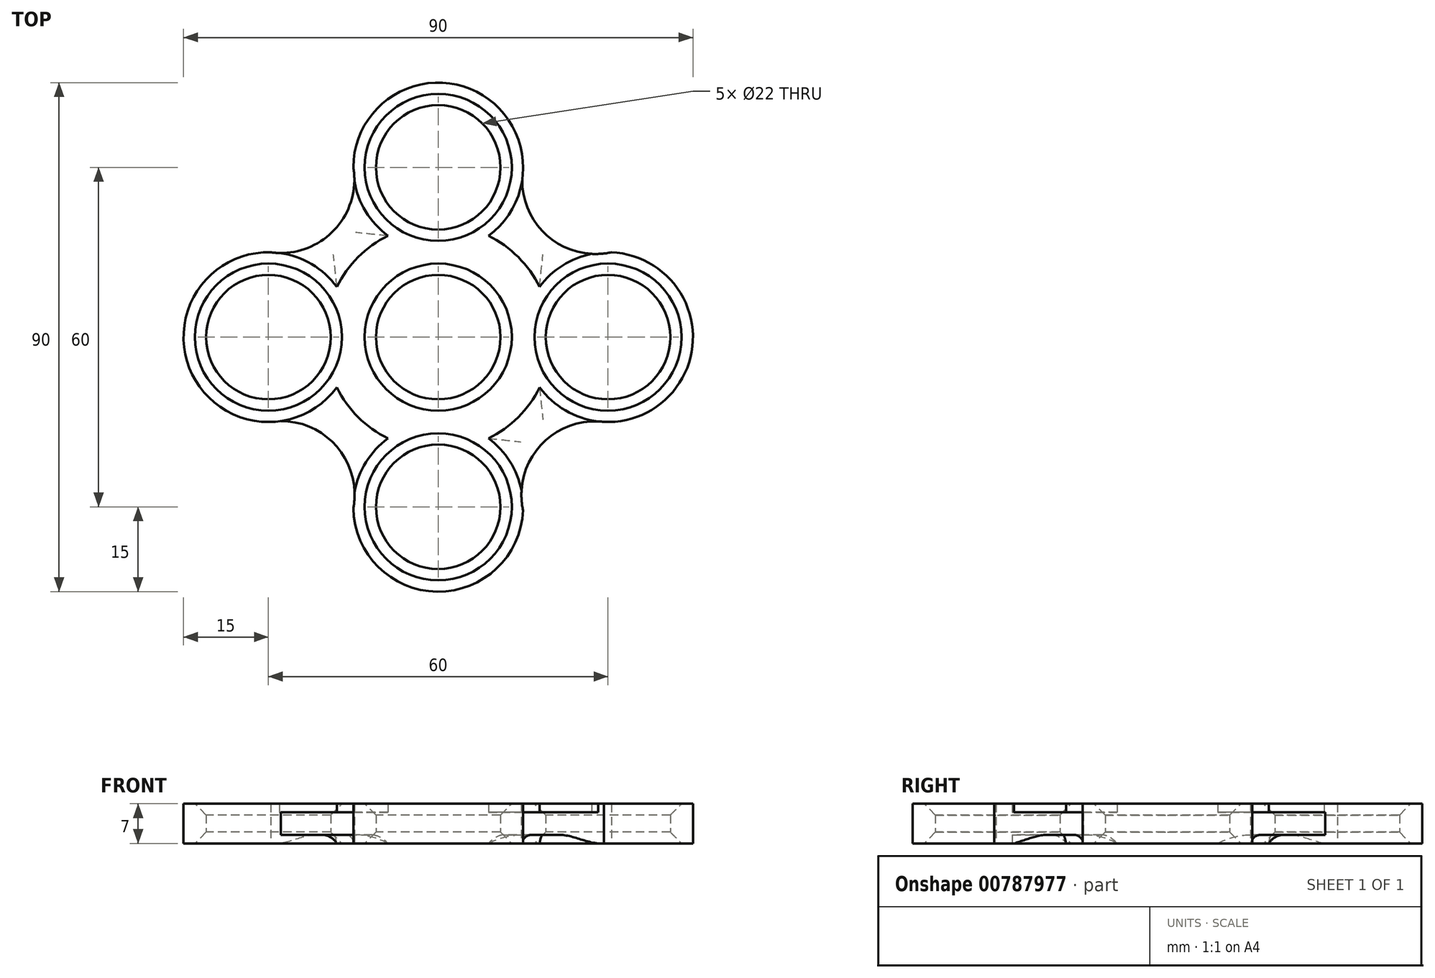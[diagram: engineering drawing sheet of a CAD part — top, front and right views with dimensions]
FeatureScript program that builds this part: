
annotation { "Feature Type Name" : "Feature", "Feature Type Description" : "" }
export const myFeature = defineFeature(function(context is Context, id is Id, definition is map)
    precondition{}
    {
        {
            var Q0;
            Q0=qCreatedBy(makeId("Top.planeOp"),FACE);
            var sketch = newSketch(context, id + "F0", { "sketchPlane" : qUnion([Q0])});
            skCircle(sketch, "E0", {"center": v(0, 0) * mm, "radius": 11 * mm});
            skCircle(sketch, "E1", {"center": v(0, 0) * mm, "radius": 20 * mm});
            skCircle(sketch, "E2", {"center": v(-30, 0) * mm, "radius": 15 * mm});
            skCircle(sketch, "E3", {"center": v(30, 0) * mm, "radius": 15 * mm});
            skCircle(sketch, "E4", {"center": v(0, 30) * mm, "radius": 15 * mm});
            skCircle(sketch, "E5", {"center": v(0, -30) * mm, "radius": 15 * mm});
            skArc(sketch, "E6", {"start": v(-29.62, 15) * mm, "mid": v(-18.5, 18.81) * mm, "end": v(-15, 30.05) * mm});
            skArc(sketch, "E7", {"start": v(14.85, 27.87) * mm, "mid": v(19.61, 17.64) * mm, "end": v(30.58, 14.99) * mm});
            skArc(sketch, "E8", {"start": v(29.26, -14.98) * mm, "mid": v(18.1, -19.12) * mm, "end": v(14.99, -30.62) * mm});
            skArc(sketch, "E9", {"start": v(-15, -30.26) * mm, "mid": v(-17.77, -19.53) * mm, "end": v(-27.82, -14.84) * mm});
            skCircle(sketch, "E10", {"center": v(0, 30) * mm, "radius": 11 * mm});
            skCircle(sketch, "E11", {"center": v(-30, 0) * mm, "radius": 11 * mm});
            skCircle(sketch, "E12", {"center": v(0, -30) * mm, "radius": 11 * mm});
            skCircle(sketch, "E13", {"center": v(30, 0) * mm, "radius": 11 * mm});
            skSolve(sketch);
        }
        {
            var Q0;
            Q0=makeQuery(id+"F0.imprint","IMPRINT",FACE,{"disambiguationData":[TD([[makeQuery(id+"F0.imprint","IMPRINT",EDGE,{"derivedFrom":sQuery(id+"F0.wireOp",EDGE,"E0")}),-1.0]])]});
            var Q1;
            {var subQ0=sQuery(id+"F0.wireOp",EDGE,"E2");var subQ3=sQuery(id+"F0.wireOp",EDGE,"E1");var subQ4=makeQuery(id+"F0.imprint","INTERSECT",VERTEX,{"disambiguationData":[OD(0.0)],"derivedFrom":[subQ3,subQ0]});Q1=makeQuery(id+"F0.imprint","IMPRINT",FACE,{"disambiguationData":[TD([[makeQuery(id+"F0.imprint","IMPRINT",EDGE,{"disambiguationData":[TD([[subQ4,-1.0]])],"derivedFrom":subQ3}),-1.0]])]});}
            var Q2;
            {var subQ0=sQuery(id+"F0.wireOp",EDGE,"E2");var subQ1=sQuery(id+"F0.wireOp",EDGE,"E1");var subQ2=makeQuery(id+"F0.imprint","INTERSECT",VERTEX,{"disambiguationData":[OD(0.0)],"derivedFrom":[subQ1,subQ0]});Q2=makeQuery(id+"F0.imprint","IMPRINT",FACE,{"disambiguationData":[TD([[makeQuery(id+"F0.imprint","IMPRINT",EDGE,{"disambiguationData":[TD([[subQ2,-1.0]])],"derivedFrom":subQ1}),1.0]])]});}
            var Q3;
            {var subQ0=sQuery(id+"F0.wireOp",EDGE,"E4");var subQ2=sQuery(id+"F0.wireOp",EDGE,"E1");var subQ7=makeQuery(id+"F0.imprint","INTERSECT",VERTEX,{"disambiguationData":[OD(0.0)],"derivedFrom":[subQ2,subQ0]});Q3=makeQuery(id+"F0.imprint","IMPRINT",FACE,{"disambiguationData":[TD([[makeQuery(id+"F0.imprint","IMPRINT",EDGE,{"disambiguationData":[TD([[subQ7,-1.0]])],"derivedFrom":subQ2}),-1.0]])]});}
            var Q4;
            {var subQ0=sQuery(id+"F0.wireOp",EDGE,"E4");var subQ1=sQuery(id+"F0.wireOp",EDGE,"E1");var subQ2=makeQuery(id+"F0.imprint","INTERSECT",VERTEX,{"disambiguationData":[OD(0.0)],"derivedFrom":[subQ1,subQ0]});Q4=makeQuery(id+"F0.imprint","IMPRINT",FACE,{"disambiguationData":[TD([[makeQuery(id+"F0.imprint","IMPRINT",EDGE,{"disambiguationData":[TD([[subQ2,-1.0]])],"derivedFrom":subQ1}),1.0]])]});}
            var Q5;
            {var subQ0=sQuery(id+"F0.wireOp",EDGE,"E3");var subQ2=sQuery(id+"F0.wireOp",EDGE,"E1");var subQ6=makeQuery(id+"F0.imprint","INTERSECT",VERTEX,{"disambiguationData":[OD(0.0)],"derivedFrom":[subQ2,subQ0]});Q5=makeQuery(id+"F0.imprint","IMPRINT",FACE,{"disambiguationData":[TD([[makeQuery(id+"F0.imprint","IMPRINT",EDGE,{"disambiguationData":[TD([[subQ6,1.0]])],"derivedFrom":subQ2}),-1.0]])]});}
            var Q6;
            {var subQ0=sQuery(id+"F0.wireOp",EDGE,"E3");var subQ1=sQuery(id+"F0.wireOp",EDGE,"E1");var subQ2=makeQuery(id+"F0.imprint","INTERSECT",VERTEX,{"disambiguationData":[OD(0.0)],"derivedFrom":[subQ1,subQ0]});Q6=makeQuery(id+"F0.imprint","IMPRINT",FACE,{"disambiguationData":[TD([[makeQuery(id+"F0.imprint","IMPRINT",EDGE,{"disambiguationData":[TD([[subQ2,1.0]])],"derivedFrom":subQ1}),1.0]])]});}
            var Q7;
            {var subQ1=sQuery(id+"F0.wireOp",EDGE,"E5");var subQ3=sQuery(id+"F0.wireOp",EDGE,"E1");var subQ4=makeQuery(id+"F0.imprint","INTERSECT",VERTEX,{"disambiguationData":[OD(0.0)],"derivedFrom":[subQ3,subQ1]});Q7=makeQuery(id+"F0.imprint","IMPRINT",FACE,{"disambiguationData":[TD([[makeQuery(id+"F0.imprint","IMPRINT",EDGE,{"disambiguationData":[TD([[subQ4,-1.0]])],"derivedFrom":subQ3}),-1.0]])]});}
            var Q8;
            {var subQ0=sQuery(id+"F0.wireOp",EDGE,"E5");var subQ1=sQuery(id+"F0.wireOp",EDGE,"E1");var subQ2=makeQuery(id+"F0.imprint","INTERSECT",VERTEX,{"disambiguationData":[OD(0.0)],"derivedFrom":[subQ1,subQ0]});Q8=makeQuery(id+"F0.imprint","IMPRINT",FACE,{"disambiguationData":[TD([[makeQuery(id+"F0.imprint","IMPRINT",EDGE,{"disambiguationData":[TD([[subQ2,-1.0]])],"derivedFrom":subQ1}),1.0]])]});}
            extrude(context, id + "F1", {"entities" : qUnion([Q0, Q1, Q2, Q3, Q4, Q5, Q6, Q7, Q8]), "depth" : 7 * mm, "offsetDistance" : 25 * mm});
        }
        {
            var Q0;
            {var subQ0=sQuery(id+"F0.wireOp",EDGE,"E2");var subQ1=sQuery(id+"F0.wireOp",EDGE,"E1");var subQ2=makeQuery(id+"F0.imprint","INTERSECT",VERTEX,{"disambiguationData":[OD(1.0)],"derivedFrom":[subQ1,subQ0]});Q0=makeQuery(id+"F0.imprint","IMPRINT",FACE,{"disambiguationData":[TD([[makeQuery(id+"F0.imprint","IMPRINT",EDGE,{"disambiguationData":[TD([[subQ2,-1.0]])],"derivedFrom":subQ1}),-1.0]])]});}
            var Q1;
            {var subQ5=sQuery(id+"F0.wireOp",EDGE,"E6");Q1=makeQuery(id+"F0.imprint","IMPRINT",FACE,{"disambiguationData":[TD([[makeQuery(id+"F0.imprint","IMPRINT",EDGE,{"derivedFrom":subQ5}),-1.0]])]});}
            var Q2;
            {var subQ0=sQuery(id+"F0.wireOp",EDGE,"E3");var subQ1=sQuery(id+"F0.wireOp",EDGE,"E1");var subQ2=makeQuery(id+"F0.imprint","INTERSECT",VERTEX,{"disambiguationData":[OD(0.0)],"derivedFrom":[subQ1,subQ0]});Q2=makeQuery(id+"F0.imprint","IMPRINT",FACE,{"disambiguationData":[TD([[makeQuery(id+"F0.imprint","IMPRINT",EDGE,{"disambiguationData":[TD([[subQ2,-1.0]])],"derivedFrom":subQ1}),-1.0]])]});}
            var Q3;
            {var subQ0=sQuery(id+"F0.wireOp",EDGE,"E5");var subQ1=sQuery(id+"F0.wireOp",EDGE,"E1");var subQ2=makeQuery(id+"F0.imprint","INTERSECT",VERTEX,{"disambiguationData":[OD(1.0)],"derivedFrom":[subQ1,subQ0]});Q3=makeQuery(id+"F0.imprint","IMPRINT",FACE,{"disambiguationData":[TD([[makeQuery(id+"F0.imprint","IMPRINT",EDGE,{"disambiguationData":[TD([[subQ2,-1.0]])],"derivedFrom":subQ1}),-1.0]])]});}
            extrude(context, id + "F2", {"entities" : qUnion([Q0, Q1, Q2, Q3]), "operationType" : NewBodyOperationType.ADD, "surfaceOperationType" : NewSurfaceOperationType.ADD, "depth" : 5.5 * mm, "offsetDistance" : 25 * mm, "hasSecondDirection" : true, "secondDirectionOppositeDirection" : false, "secondDirectionDepth" : 1.5 * mm});
        }
        {
            var Q0;
            {var subQ0=sQuery(id+"F0.wireOp",EDGE,"E1");Q0=makeQuery(id+"F2.opExtrude","CAP_EDGE",EDGE,{"disambiguationData":[OSD([subQ0]),TDD([makeQuery(id+"F0.imprint","IMPRINT",EDGE,{"disambiguationData":[TD([[makeQuery(id+"F0.imprint","INTERSECT",VERTEX,{"disambiguationData":[OD(1.0)],"derivedFrom":[subQ0,sQuery(id+"F0.wireOp",EDGE,"E2")]}),-1.0]])],"derivedFrom":subQ0})])],"isStart":false});}
            var Q1;
            {var subQ0=sQuery(id+"F0.wireOp",EDGE,"E1");Q1=makeQuery(id+"F2.opExtrude","CAP_EDGE",EDGE,{"disambiguationData":[OSD([subQ0]),TDD([makeQuery(id+"F0.imprint","IMPRINT",EDGE,{"disambiguationData":[TD([[makeQuery(id+"F0.imprint","INTERSECT",VERTEX,{"disambiguationData":[OD(1.0)],"derivedFrom":[subQ0,sQuery(id+"F0.wireOp",EDGE,"E2")]}),-1.0]])],"derivedFrom":subQ0})])],"isStart":true});}
            var Q2;
            {var subQ0=sQuery(id+"F0.wireOp",EDGE,"E1");Q2=makeQuery(id+"F2.opExtrude","CAP_EDGE",EDGE,{"disambiguationData":[OSD([subQ0]),TDD([makeQuery(id+"F0.imprint","IMPRINT",EDGE,{"disambiguationData":[TD([[makeQuery(id+"F0.imprint","INTERSECT",VERTEX,{"disambiguationData":[OD(1.0)],"derivedFrom":[subQ0,sQuery(id+"F0.wireOp",EDGE,"E4")]}),-1.0]])],"derivedFrom":subQ0})])],"isStart":false});}
            var Q3;
            {var subQ0=sQuery(id+"F0.wireOp",EDGE,"E1");Q3=makeQuery(id+"F2.opExtrude","CAP_EDGE",EDGE,{"disambiguationData":[OSD([subQ0]),TDD([makeQuery(id+"F0.imprint","IMPRINT",EDGE,{"disambiguationData":[TD([[makeQuery(id+"F0.imprint","INTERSECT",VERTEX,{"disambiguationData":[OD(1.0)],"derivedFrom":[subQ0,sQuery(id+"F0.wireOp",EDGE,"E4")]}),-1.0]])],"derivedFrom":subQ0})])],"isStart":true});}
            var Q4;
            {var subQ0=sQuery(id+"F0.wireOp",EDGE,"E1");Q4=makeQuery(id+"F2.opExtrude","CAP_EDGE",EDGE,{"disambiguationData":[OSD([subQ0]),TDD([makeQuery(id+"F0.imprint","IMPRINT",EDGE,{"disambiguationData":[TD([[makeQuery(id+"F0.imprint","INTERSECT",VERTEX,{"disambiguationData":[OD(0.0)],"derivedFrom":[subQ0,sQuery(id+"F0.wireOp",EDGE,"E3")]}),-1.0]])],"derivedFrom":subQ0})])],"isStart":false});}
            var Q5;
            {var subQ0=sQuery(id+"F0.wireOp",EDGE,"E1");Q5=makeQuery(id+"F2.opExtrude","CAP_EDGE",EDGE,{"disambiguationData":[OSD([subQ0]),TDD([makeQuery(id+"F0.imprint","IMPRINT",EDGE,{"disambiguationData":[TD([[makeQuery(id+"F0.imprint","INTERSECT",VERTEX,{"disambiguationData":[OD(0.0)],"derivedFrom":[subQ0,sQuery(id+"F0.wireOp",EDGE,"E3")]}),-1.0]])],"derivedFrom":subQ0})])],"isStart":true});}
            var Q6;
            {var subQ0=sQuery(id+"F0.wireOp",EDGE,"E1");Q6=makeQuery(id+"F2.opExtrude","CAP_EDGE",EDGE,{"disambiguationData":[OSD([subQ0]),TDD([makeQuery(id+"F0.imprint","IMPRINT",EDGE,{"disambiguationData":[TD([[makeQuery(id+"F0.imprint","INTERSECT",VERTEX,{"disambiguationData":[OD(1.0)],"derivedFrom":[subQ0,sQuery(id+"F0.wireOp",EDGE,"E5")]}),-1.0]])],"derivedFrom":subQ0})])],"isStart":false});}
            var Q7;
            {var subQ0=sQuery(id+"F0.wireOp",EDGE,"E1");Q7=makeQuery(id+"F2.opExtrude","CAP_EDGE",EDGE,{"disambiguationData":[OSD([subQ0]),TDD([makeQuery(id+"F0.imprint","IMPRINT",EDGE,{"disambiguationData":[TD([[makeQuery(id+"F0.imprint","INTERSECT",VERTEX,{"disambiguationData":[OD(1.0)],"derivedFrom":[subQ0,sQuery(id+"F0.wireOp",EDGE,"E5")]}),-1.0]])],"derivedFrom":subQ0})])],"isStart":true});}
            var Q8;
            {var subQ0=sQuery(id+"F0.wireOp",EDGE,"E5");Q8=makeQuery(id+"F2.opExtrude","CAP_EDGE",EDGE,{"disambiguationData":[OSD([subQ0]),TDD([makeQuery(id+"F0.imprint","IMPRINT",EDGE,{"disambiguationData":[TD([[makeQuery(id+"F0.imprint","INTERSECT",VERTEX,{"disambiguationData":[OD(1.0)],"derivedFrom":[subQ0,sQuery(id+"F0.wireOp",EDGE,"E8")]}),-1.0]])],"derivedFrom":subQ0})])],"isStart":false});}
            var Q9;
            {var subQ0=sQuery(id+"F0.wireOp",EDGE,"E3");Q9=makeQuery(id+"F2.opExtrude","CAP_EDGE",EDGE,{"disambiguationData":[OSD([subQ0]),TDD([makeQuery(id+"F0.imprint","IMPRINT",EDGE,{"disambiguationData":[TD([[makeQuery(id+"F0.imprint","INTERSECT",VERTEX,{"derivedFrom":[subQ0,sQuery(id+"F0.wireOp",EDGE,"E8")]}),1.0]])],"derivedFrom":subQ0})])],"isStart":false});}
            var Q10;
            {var subQ0=sQuery(id+"F0.wireOp",EDGE,"E5");Q10=makeQuery(id+"F2.opExtrude","CAP_EDGE",EDGE,{"disambiguationData":[OSD([subQ0]),TDD([makeQuery(id+"F0.imprint","IMPRINT",EDGE,{"disambiguationData":[TD([[makeQuery(id+"F0.imprint","INTERSECT",VERTEX,{"disambiguationData":[OD(1.0)],"derivedFrom":[subQ0,sQuery(id+"F0.wireOp",EDGE,"E8")]}),-1.0]])],"derivedFrom":subQ0})])],"isStart":true});}
            var Q11;
            {var subQ0=sQuery(id+"F0.wireOp",EDGE,"E3");Q11=makeQuery(id+"F2.opExtrude","CAP_EDGE",EDGE,{"disambiguationData":[OSD([subQ0]),TDD([makeQuery(id+"F0.imprint","IMPRINT",EDGE,{"disambiguationData":[TD([[makeQuery(id+"F0.imprint","INTERSECT",VERTEX,{"derivedFrom":[subQ0,sQuery(id+"F0.wireOp",EDGE,"E8")]}),1.0]])],"derivedFrom":subQ0})])],"isStart":true});}
            var Q12;
            {var subQ0=sQuery(id+"F0.wireOp",EDGE,"E2");Q12=makeQuery(id+"F2.opExtrude","CAP_EDGE",EDGE,{"disambiguationData":[OSD([subQ0]),TDD([makeQuery(id+"F0.imprint","IMPRINT",EDGE,{"disambiguationData":[TD([[makeQuery(id+"F0.imprint","INTERSECT",VERTEX,{"derivedFrom":[subQ0,sQuery(id+"F0.wireOp",EDGE,"E9")]}),-1.0]])],"derivedFrom":subQ0})])],"isStart":true});}
            var Q13;
            {var subQ0=sQuery(id+"F0.wireOp",EDGE,"E5");Q13=makeQuery(id+"F2.opExtrude","CAP_EDGE",EDGE,{"disambiguationData":[OSD([subQ0]),TDD([makeQuery(id+"F0.imprint","IMPRINT",EDGE,{"disambiguationData":[TD([[makeQuery(id+"F0.imprint","INTERSECT",VERTEX,{"disambiguationData":[OD(1.0)],"derivedFrom":[subQ0,sQuery(id+"F0.wireOp",EDGE,"E9")]}),1.0]])],"derivedFrom":subQ0})])],"isStart":true});}
            var Q14;
            {var subQ0=sQuery(id+"F0.wireOp",EDGE,"E2");Q14=makeQuery(id+"F2.opExtrude","CAP_EDGE",EDGE,{"disambiguationData":[OSD([subQ0]),TDD([makeQuery(id+"F0.imprint","IMPRINT",EDGE,{"disambiguationData":[TD([[makeQuery(id+"F0.imprint","INTERSECT",VERTEX,{"derivedFrom":[subQ0,sQuery(id+"F0.wireOp",EDGE,"E9")]}),-1.0]])],"derivedFrom":subQ0})])],"isStart":false});}
            var Q15;
            {var subQ0=sQuery(id+"F0.wireOp",EDGE,"E5");Q15=makeQuery(id+"F2.opExtrude","CAP_EDGE",EDGE,{"disambiguationData":[OSD([subQ0]),TDD([makeQuery(id+"F0.imprint","IMPRINT",EDGE,{"disambiguationData":[TD([[makeQuery(id+"F0.imprint","INTERSECT",VERTEX,{"disambiguationData":[OD(1.0)],"derivedFrom":[subQ0,sQuery(id+"F0.wireOp",EDGE,"E9")]}),1.0]])],"derivedFrom":subQ0})])],"isStart":false});}
            var Q16;
            {var subQ0=sQuery(id+"F0.wireOp",EDGE,"E4");Q16=makeQuery(id+"F2.opExtrude","CAP_EDGE",EDGE,{"disambiguationData":[OSD([subQ0]),TDD([makeQuery(id+"F0.imprint","IMPRINT",EDGE,{"disambiguationData":[TD([[makeQuery(id+"F0.imprint","INTERSECT",VERTEX,{"derivedFrom":[subQ0,sQuery(id+"F0.wireOp",EDGE,"E6")]}),-1.0]])],"derivedFrom":subQ0})])],"isStart":false});}
            var Q17;
            {var subQ0=sQuery(id+"F0.wireOp",EDGE,"E2");Q17=makeQuery(id+"F2.opExtrude","CAP_EDGE",EDGE,{"disambiguationData":[OSD([subQ0]),TDD([makeQuery(id+"F0.imprint","IMPRINT",EDGE,{"disambiguationData":[TD([[makeQuery(id+"F0.imprint","INTERSECT",VERTEX,{"derivedFrom":[subQ0,sQuery(id+"F0.wireOp",EDGE,"E6")]}),1.0]])],"derivedFrom":subQ0})])],"isStart":false});}
            var Q18;
            {var subQ0=sQuery(id+"F0.wireOp",EDGE,"E4");Q18=makeQuery(id+"F2.opExtrude","CAP_EDGE",EDGE,{"disambiguationData":[OSD([subQ0]),TDD([makeQuery(id+"F0.imprint","IMPRINT",EDGE,{"disambiguationData":[TD([[makeQuery(id+"F0.imprint","INTERSECT",VERTEX,{"derivedFrom":[subQ0,sQuery(id+"F0.wireOp",EDGE,"E6")]}),-1.0]])],"derivedFrom":subQ0})])],"isStart":true});}
            var Q19;
            {var subQ0=sQuery(id+"F0.wireOp",EDGE,"E2");Q19=makeQuery(id+"F2.opExtrude","CAP_EDGE",EDGE,{"disambiguationData":[OSD([subQ0]),TDD([makeQuery(id+"F0.imprint","IMPRINT",EDGE,{"disambiguationData":[TD([[makeQuery(id+"F0.imprint","INTERSECT",VERTEX,{"derivedFrom":[subQ0,sQuery(id+"F0.wireOp",EDGE,"E6")]}),1.0]])],"derivedFrom":subQ0})])],"isStart":true});}
            var Q20;
            {var subQ0=sQuery(id+"F0.wireOp",EDGE,"E3");Q20=makeQuery(id+"F2.opExtrude","CAP_EDGE",EDGE,{"disambiguationData":[OSD([subQ0]),TDD([makeQuery(id+"F0.imprint","IMPRINT",EDGE,{"disambiguationData":[TD([[makeQuery(id+"F0.imprint","INTERSECT",VERTEX,{"disambiguationData":[OD(1.0)],"derivedFrom":[subQ0,sQuery(id+"F0.wireOp",EDGE,"E7")]}),-1.0]])],"derivedFrom":subQ0})])],"isStart":false});}
            var Q21;
            {var subQ0=sQuery(id+"F0.wireOp",EDGE,"E4");Q21=makeQuery(id+"F2.opExtrude","CAP_EDGE",EDGE,{"disambiguationData":[OSD([subQ0]),TDD([makeQuery(id+"F0.imprint","IMPRINT",EDGE,{"disambiguationData":[TD([[makeQuery(id+"F0.imprint","INTERSECT",VERTEX,{"derivedFrom":[subQ0,sQuery(id+"F0.wireOp",EDGE,"E7")]}),1.0]])],"derivedFrom":subQ0})])],"isStart":false});}
            var Q22;
            {var subQ0=sQuery(id+"F0.wireOp",EDGE,"E3");Q22=makeQuery(id+"F2.opExtrude","CAP_EDGE",EDGE,{"disambiguationData":[OSD([subQ0]),TDD([makeQuery(id+"F0.imprint","IMPRINT",EDGE,{"disambiguationData":[TD([[makeQuery(id+"F0.imprint","INTERSECT",VERTEX,{"disambiguationData":[OD(1.0)],"derivedFrom":[subQ0,sQuery(id+"F0.wireOp",EDGE,"E7")]}),-1.0]])],"derivedFrom":subQ0})])],"isStart":true});}
            var Q23;
            {var subQ0=sQuery(id+"F0.wireOp",EDGE,"E4");Q23=makeQuery(id+"F2.opExtrude","CAP_EDGE",EDGE,{"disambiguationData":[OSD([subQ0]),TDD([makeQuery(id+"F0.imprint","IMPRINT",EDGE,{"disambiguationData":[TD([[makeQuery(id+"F0.imprint","INTERSECT",VERTEX,{"derivedFrom":[subQ0,sQuery(id+"F0.wireOp",EDGE,"E7")]}),1.0]])],"derivedFrom":subQ0})])],"isStart":true});}
            fillet(context, id + "F3", {"entities" : qUnion([Q0, Q1, Q2, Q3, Q4, Q5, Q6, Q7, Q8, Q9, Q10, Q11, Q12, Q13, Q14, Q15, Q16, Q17, Q18, Q19, Q20, Q21, Q22, Q23]), "radius" : 5 * mm, "tangentPropagation" : true, "allowEdgeOverflow" : false});
        }
        {
            var Q0;
            Q0=makeQuery(id+"F1.opExtrude","CAP_EDGE",EDGE,{"disambiguationData":[OSD([sQuery(id+"F0.wireOp",EDGE,"E13")])],"isStart":false});
            var Q1;
            Q1=makeQuery(id+"F1.opExtrude","CAP_EDGE",EDGE,{"disambiguationData":[OSD([sQuery(id+"F0.wireOp",EDGE,"E12")])],"isStart":false});
            var Q2;
            Q2=makeQuery(id+"F1.opExtrude","CAP_EDGE",EDGE,{"disambiguationData":[OSD([sQuery(id+"F0.wireOp",EDGE,"E11")])],"isStart":false});
            var Q3;
            Q3=makeQuery(id+"F1.opExtrude","CAP_EDGE",EDGE,{"disambiguationData":[OSD([sQuery(id+"F0.wireOp",EDGE,"E10")])],"isStart":false});
            var Q4;
            Q4=makeQuery(id+"F1.opExtrude","CAP_EDGE",EDGE,{"disambiguationData":[OSD([sQuery(id+"F0.wireOp",EDGE,"E0")])],"isStart":false});
            var Q5;
            Q5=makeQuery(id+"F1.opExtrude","CAP_EDGE",EDGE,{"disambiguationData":[OSD([sQuery(id+"F0.wireOp",EDGE,"E13")])],"isStart":true});
            var Q6;
            Q6=makeQuery(id+"F1.opExtrude","CAP_EDGE",EDGE,{"disambiguationData":[OSD([sQuery(id+"F0.wireOp",EDGE,"E0")])],"isStart":true});
            var Q7;
            Q7=makeQuery(id+"F1.opExtrude","CAP_EDGE",EDGE,{"disambiguationData":[OSD([sQuery(id+"F0.wireOp",EDGE,"E11")])],"isStart":true});
            var Q8;
            Q8=makeQuery(id+"F1.opExtrude","CAP_EDGE",EDGE,{"disambiguationData":[OSD([sQuery(id+"F0.wireOp",EDGE,"E12")])],"isStart":true});
            var Q9;
            Q9=makeQuery(id+"F1.opExtrude","CAP_EDGE",EDGE,{"disambiguationData":[OSD([sQuery(id+"F0.wireOp",EDGE,"E10")])],"isStart":true});
            chamfer(context, id + "F4", {"entities" : qUnion([Q0, Q1, Q2, Q3, Q4, Q5, Q6, Q7, Q8, Q9]), "width" : 2 * mm, "tangentPropagation" : true});
        }
    });
